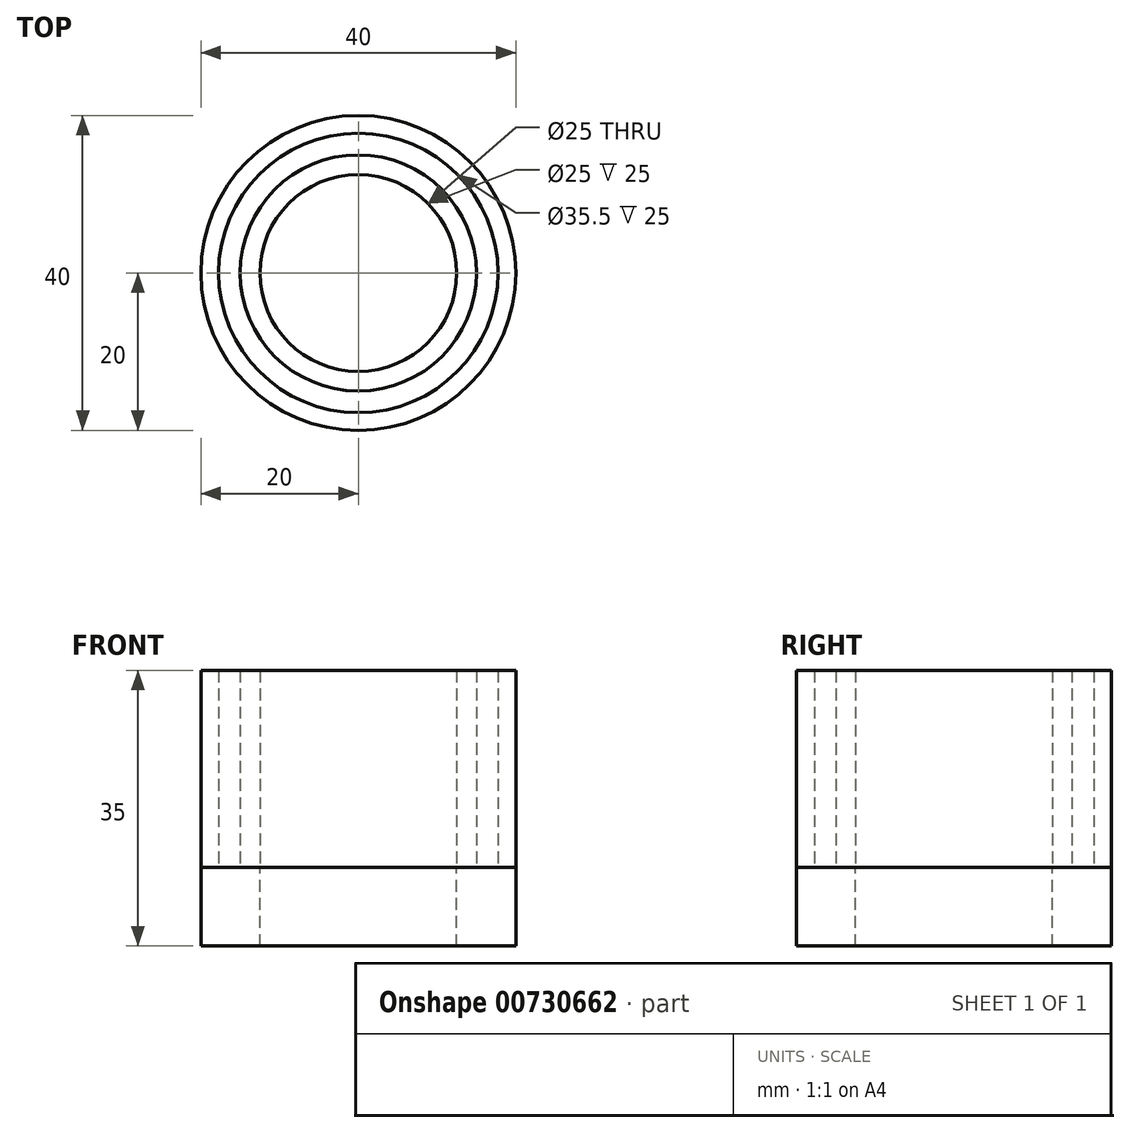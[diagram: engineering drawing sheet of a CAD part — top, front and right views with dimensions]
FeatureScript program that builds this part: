
annotation { "Feature Type Name" : "Feature", "Feature Type Description" : "" }
export const myFeature = defineFeature(function(context is Context, id is Id, definition is map)
    precondition{}
    {
        {
            var Q0;
            Q0=qCreatedBy(makeId("Top.planeOp"),FACE);
            var sketch = newSketch(context, id + "F0", { "sketchPlane" : qUnion([Q0])});
            skCircle(sketch, "E0", {"center": v(0, 0) * mm, "radius": 12.5 * mm});
            skCircle(sketch, "E1", {"center": v(0, 0) * mm, "radius": 15 * mm});
            skCircle(sketch, "E2", {"center": v(0, 0) * mm, "radius": 17.75 * mm});
            skCircle(sketch, "E3", {"center": v(0, 0) * mm, "radius": 20 * mm});
            skSolve(sketch);
        }
        {
            var Q0;
            Q0=makeQuery(id+"F0.imprint","IMPRINT",FACE,{"disambiguationData":[TD([[makeQuery(id+"F0.imprint","IMPRINT",EDGE,{"derivedFrom":sQuery(id+"F0.wireOp",EDGE,"E0")}),-1.0]])]});
            var Q1;
            Q1=makeQuery(id+"F0.imprint","IMPRINT",FACE,{"disambiguationData":[TD([[makeQuery(id+"F0.imprint","IMPRINT",EDGE,{"derivedFrom":sQuery(id+"F0.wireOp",EDGE,"E2")}),-1.0]])]});
            extrude(context, id + "F1", {"entities" : qUnion([Q0, Q1]), "depth" : 25 * mm, "offsetDistance" : 25 * mm});
        }
        {
            var Q0;
            Q0=qCreatedBy(makeId("Top.planeOp"),FACE);
            var sketch = newSketch(context, id + "F2", { "sketchPlane" : qUnion([Q0])});
            skCircle(sketch, "E4", {"center": v(0, 0) * mm, "radius": 12.5 * mm});
            skCircle(sketch, "E5", {"center": v(0, 0) * mm, "radius": 20 * mm});
            skSolve(sketch);
        }
        {
            var Q0;
            Q0 = qSketchRegion(id + "F2", true);
            extrude(context, id + "F3", {"entities" : qUnion([Q0]), "depth" : 0 * mm, "offsetDistance" : 25 * mm, "hasSecondDirection" : true, "secondDirectionOppositeDirection" : true, "secondDirectionDepth" : 10 * mm});
        }
    });
